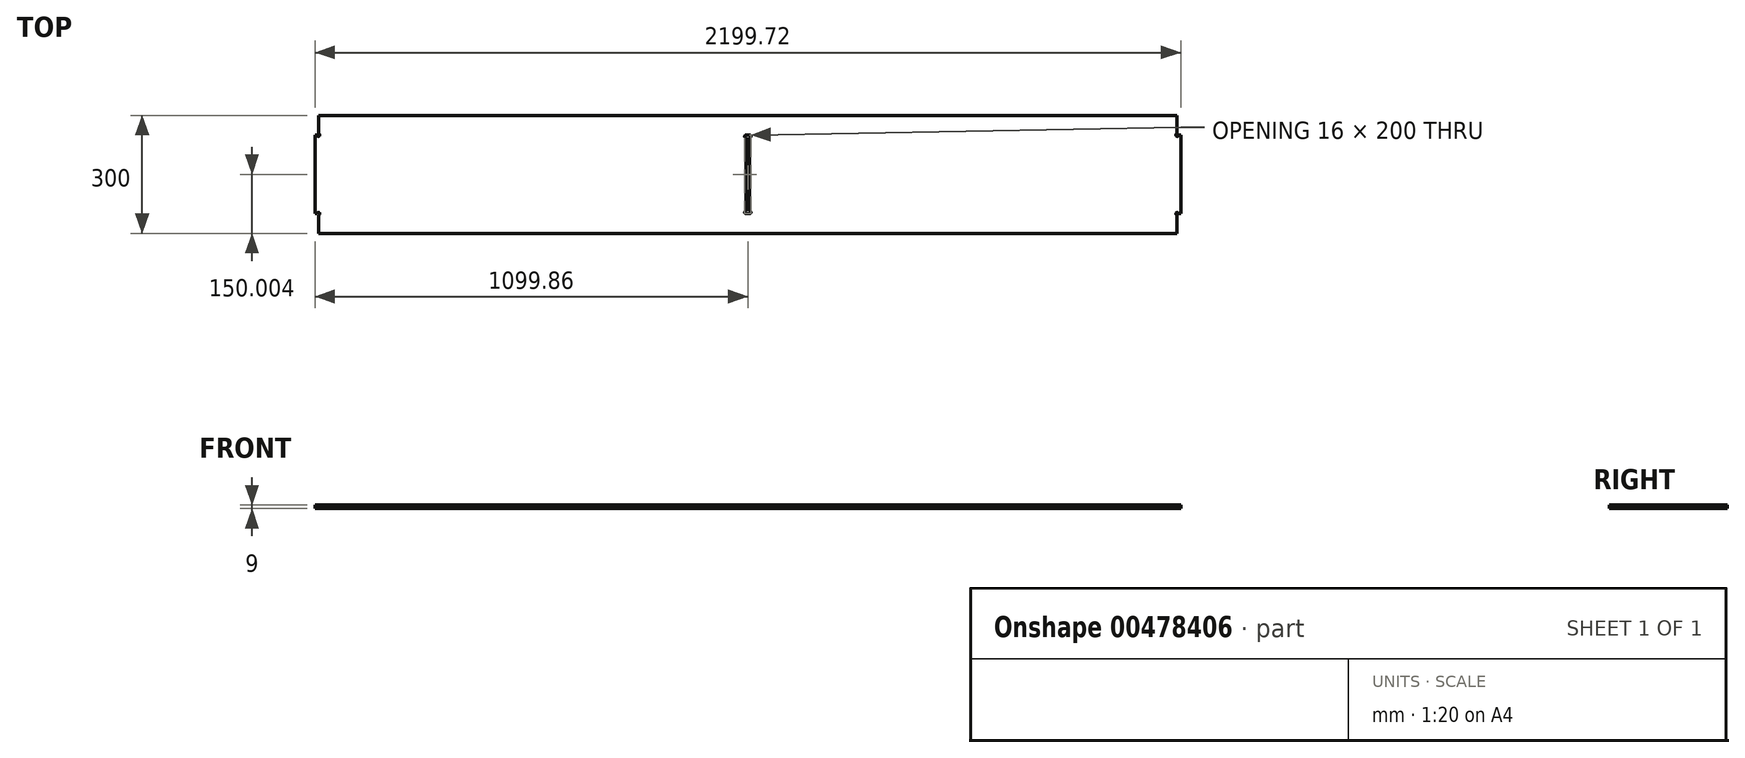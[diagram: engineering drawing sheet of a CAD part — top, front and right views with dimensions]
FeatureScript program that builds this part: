
annotation { "Feature Type Name" : "Feature", "Feature Type Description" : "" }
export const myFeature = defineFeature(function(context is Context, id is Id, definition is map)
    precondition{}
    {
        {
            var Q0;
            Q0=qCreatedBy(makeId("Top.planeOp"),FACE);
            var sketch = newSketch(context, id + "F0", { "sketchPlane" : qUnion([Q0])});
            skLineSegment(sketch, "E0.bottom", {"start": v(-1090.86, -105.8) * mm, "end": v(1091.14, -105.8) * mm});
            skLineSegment(sketch, "E0.top", {"start": v(-1090.86, -405.8) * mm, "end": v(1091.14, -405.8) * mm});
            skLineSegment(sketch, "E0.left", {"start": v(-1090.86, -105.8) * mm, "end": v(-1090.86, -152.3) * mm});
            skLineSegment(sketch, "E1.0", {"start": v(-1099.86, -155.8) * mm, "end": v(-1099.86, -355.8) * mm});
            skLineSegment(sketch, "E2", {"start": v(-1099.86, -155.8) * mm, "end": v(-1094.36, -155.8) * mm});
            skLineSegment(sketch, "E3", {"start": v(-1094.36, -355.8) * mm, "end": v(-1099.86, -355.8) * mm});
            skArc(sketch, "E4", {"start": v(-1094.36, -355.8) * mm, "mid": v(-1093.33, -353.32) * mm, "end": v(-1090.86, -352.3) * mm});
            skArc(sketch, "E5", {"start": v(-1090.86, -352.3) * mm, "mid": v(-1088.38, -353.32) * mm, "end": v(-1087.36, -355.8) * mm});
            skArc(sketch, "E6", {"start": v(-1087.36, -355.8) * mm, "mid": v(-1088.38, -358.27) * mm, "end": v(-1090.86, -359.3) * mm});
            skLineSegment(sketch, "E7.trimOffspring", {"start": v(-1090.86, -359.3) * mm, "end": v(-1090.86, -405.8) * mm});
            skArc(sketch, "E8", {"start": v(-1094.36, -155.8) * mm, "mid": v(-1088.38, -158.27) * mm, "end": v(-1090.86, -152.3) * mm});
            skLineSegment(sketch, "E9.0", {"start": v(0, -159.3) * mm, "end": v(0, -352.3) * mm, "construction": true});
            skLineSegment(sketch, "E10.MirrorCS", {"start": v(1090.86, -359.3) * mm, "end": v(1090.86, -405.8) * mm});
            skArc(sketch, "E11.MirrorCS", {"start": v(1087.36, -355.8) * mm, "mid": v(1088.38, -358.27) * mm, "end": v(1090.86, -359.3) * mm});
            skLineSegment(sketch, "E12.MirrorCS", {"start": v(1094.36, -355.8) * mm, "end": v(1099.86, -355.8) * mm});
            skLineSegment(sketch, "E13.MirrorCS", {"start": v(1099.86, -155.8) * mm, "end": v(1099.86, -355.8) * mm});
            skLineSegment(sketch, "E14.MirrorCS", {"start": v(1099.86, -155.8) * mm, "end": v(1094.36, -155.8) * mm});
            skArc(sketch, "E15.MirrorCS", {"start": v(1094.36, -155.8) * mm, "mid": v(1088.38, -158.27) * mm, "end": v(1090.86, -152.3) * mm});
            skLineSegment(sketch, "E16.MirrorCS", {"start": v(1090.86, -105.8) * mm, "end": v(1090.86, -152.3) * mm});
            skArc(sketch, "E17.MirrorCS", {"start": v(1090.86, -352.3) * mm, "mid": v(1088.38, -353.32) * mm, "end": v(1087.36, -355.8) * mm});
            skArc(sketch, "E18.MirrorCS", {"start": v(1094.36, -355.8) * mm, "mid": v(1093.33, -353.32) * mm, "end": v(1090.86, -352.3) * mm});
            skLineSegment(sketch, "E19.0", {"start": v(-1091, -255.8) * mm, "end": v(1091, -255.8) * mm, "construction": true});
            skLineSegment(sketch, "E20.0", {"start": v(4.5, -162.8) * mm, "end": v(4.5, -255.8) * mm});
            skLineSegment(sketch, "E21", {"start": v(4.5, -155.8) * mm, "end": v(0, -155.8) * mm});
            skArc(sketch, "E22", {"start": v(4.5, -162.8) * mm, "mid": v(8, -159.3) * mm, "end": v(4.5, -155.8) * mm});
            skLineSegment(sketch, "E23.MirrorCS", {"start": v(-4.5, -155.8) * mm, "end": v(0, -155.8) * mm});
            skArc(sketch, "E24.MirrorCS", {"start": v(-4.5, -162.8) * mm, "mid": v(-8, -159.3) * mm, "end": v(-4.5, -155.8) * mm});
            skLineSegment(sketch, "E25.MirrorCS", {"start": v(-4.5, -162.8) * mm, "end": v(-4.5, -255.8) * mm});
            skArc(sketch, "E26.MirrorCS", {"start": v(-4.5, -348.8) * mm, "mid": v(-8, -352.3) * mm, "end": v(-4.5, -355.8) * mm});
            skLineSegment(sketch, "E27.MirrorCS", {"start": v(-4.5, -355.8) * mm, "end": v(0, -355.8) * mm});
            skLineSegment(sketch, "E28.MirrorCS", {"start": v(4.5, -355.8) * mm, "end": v(0, -355.8) * mm});
            skArc(sketch, "E29.MirrorCS", {"start": v(4.5, -348.8) * mm, "mid": v(8, -352.3) * mm, "end": v(4.5, -355.8) * mm});
            skLineSegment(sketch, "E30.MirrorCS", {"start": v(4.5, -348.8) * mm, "end": v(4.5, -255.8) * mm});
            skLineSegment(sketch, "E31.MirrorCS", {"start": v(-4.5, -348.8) * mm, "end": v(-4.5, -255.8) * mm});
            skSolve(sketch);
        }
        {
            var Q0;
            Q0=makeQuery(id+"F0.imprint","IMPRINT",FACE,{"disambiguationData":[TD([[makeQuery(id+"F0.imprint","IMPRINT",EDGE,{"derivedFrom":sQuery(id+"F0.wireOp",EDGE,"E0.bottom")}),-1.0]])]});
            extrude(context, id + "F1", {"entities" : qUnion([Q0]), "depth" : 9 * mm});
        }
    });
